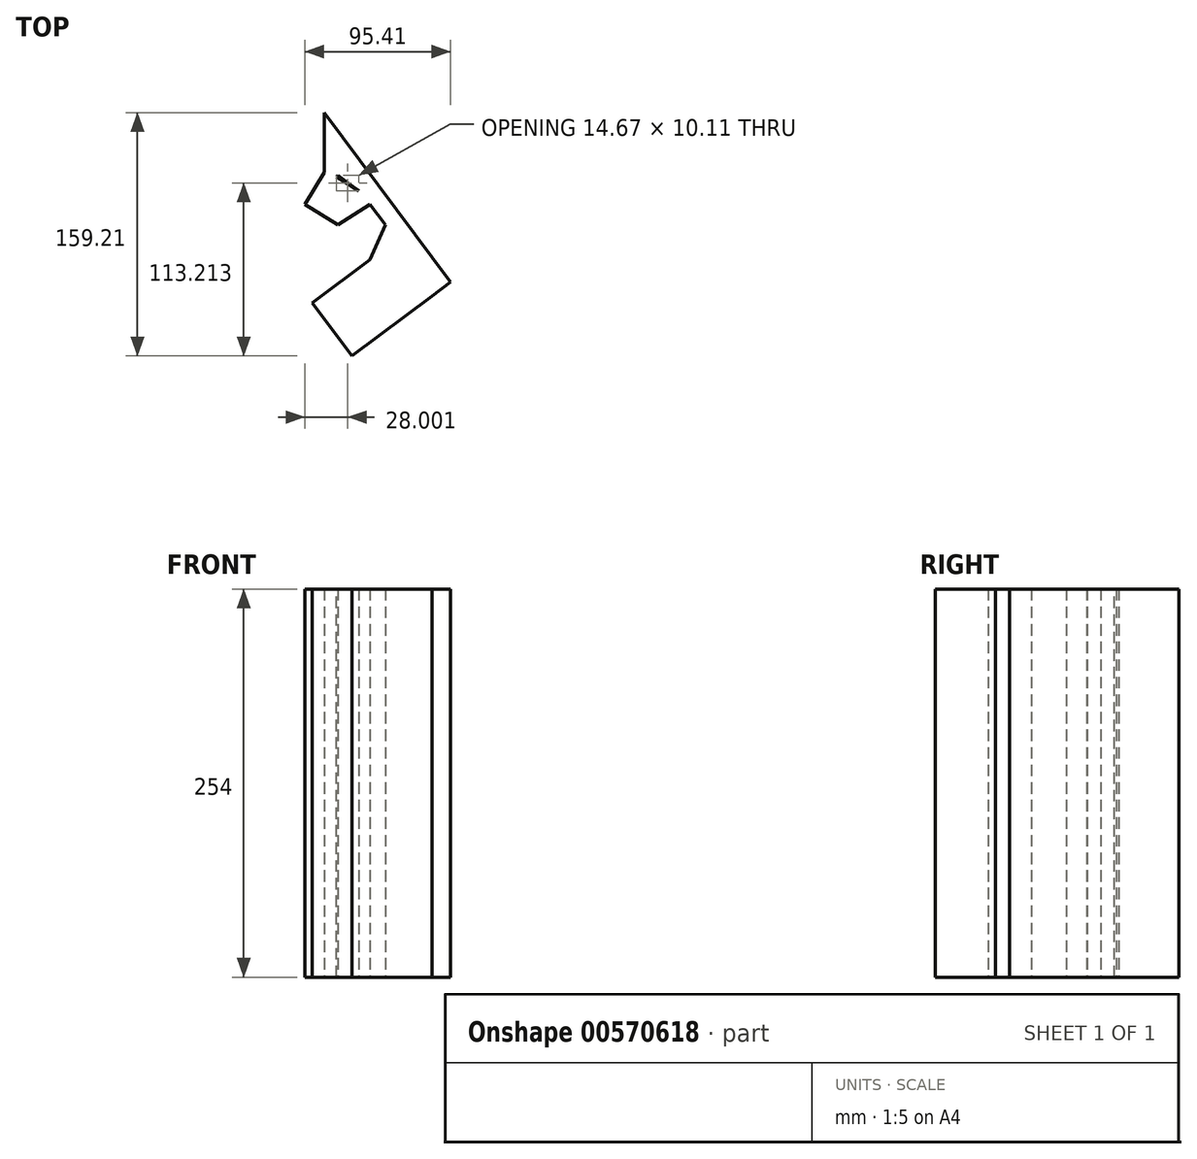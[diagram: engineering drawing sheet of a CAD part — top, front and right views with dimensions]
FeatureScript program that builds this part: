
annotation { "Feature Type Name" : "Feature", "Feature Type Description" : "" }
export const myFeature = defineFeature(function(context is Context, id is Id, definition is map)
    precondition{}
    {
        {
            var Q0;
            Q0=qCreatedBy(makeId("Top.planeOp"),FACE);
            var sketch = newSketch(context, id + "F0", { "sketchPlane" : qUnion([Q0])});
            skLineSegment(sketch, "E0", {"start": v(-123.35, 112.76) * mm, "end": v(-40.77, 2.01) * mm});
            skLineSegment(sketch, "E1", {"start": v(-123.35, 112.76) * mm, "end": v(-123.35, 61.7) * mm});
            skLineSegment(sketch, "E2", {"start": v(-123.35, 61.7) * mm, "end": v(-114.5, 71.82) * mm});
            skLineSegment(sketch, "E3", {"start": v(-114.5, 71.82) * mm, "end": v(-100.84, 61.7) * mm});
            skLineSegment(sketch, "E4", {"start": v(-100.84, 61.7) * mm, "end": v(-114.5, 39.34) * mm});
            skLineSegment(sketch, "E5", {"start": v(-114.5, 39.34) * mm, "end": v(-93.59, 52.72) * mm});
            skLineSegment(sketch, "E6", {"start": v(-93.59, 52.72) * mm, "end": v(-83.61, 39.34) * mm});
            skLineSegment(sketch, "E7", {"start": v(-83.61, 39.34) * mm, "end": v(-93.59, 16.38) * mm});
            skLineSegment(sketch, "E8", {"start": v(-93.59, 16.38) * mm, "end": v(-78.77, 27.43) * mm});
            skLineSegment(sketch, "E9", {"start": v(-78.77, 27.43) * mm, "end": v(-52.89, -7.28) * mm});
            skLineSegment(sketch, "E10", {"start": v(-52.89, -7.28) * mm, "end": v(-40.77, 2.01) * mm});
            skSolve(sketch);
        }
        {
            var Q0;
            Q0=makeQuery(id+"F0.imprint","IMPRINT",FACE,{"disambiguationData":[TD([[makeQuery(id+"F0.imprint","IMPRINT",EDGE,{"derivedFrom":sQuery(id+"F0.wireOp",EDGE,"E0")}),-1.0]])]});
            extrude(context, id + "F1", {"entities" : qUnion([Q0]), "depth" : 254 * mm, "offsetDistance" : 25.4 * mm});
        }
        {
            var Q0;
            Q0=makeQuery(id+"F1.opExtrude","SWEPT_FACE",FACE,{"disambiguationData":[OSD([sQuery(id+"F0.wireOp",EDGE,"E9")])]});
            extrude(context, id + "F2", {"entities" : qUnion([Q0]), "operationType" : NewBodyOperationType.ADD, "depth" : 65.53 * mm, "offsetDistance" : 25.4 * mm});
        }
        {
            var Q0;
            Q0=makeQuery(id+"F1.opExtrude","SWEPT_FACE",FACE,{"disambiguationData":[OSD([sQuery(id+"F0.wireOp",EDGE,"E4")])]});
            extrude(context, id + "F3", {"entities" : qUnion([Q0]), "operationType" : NewBodyOperationType.ADD, "depth" : 25.4 * mm, "offsetDistance" : 25.4 * mm});
        }
    });
